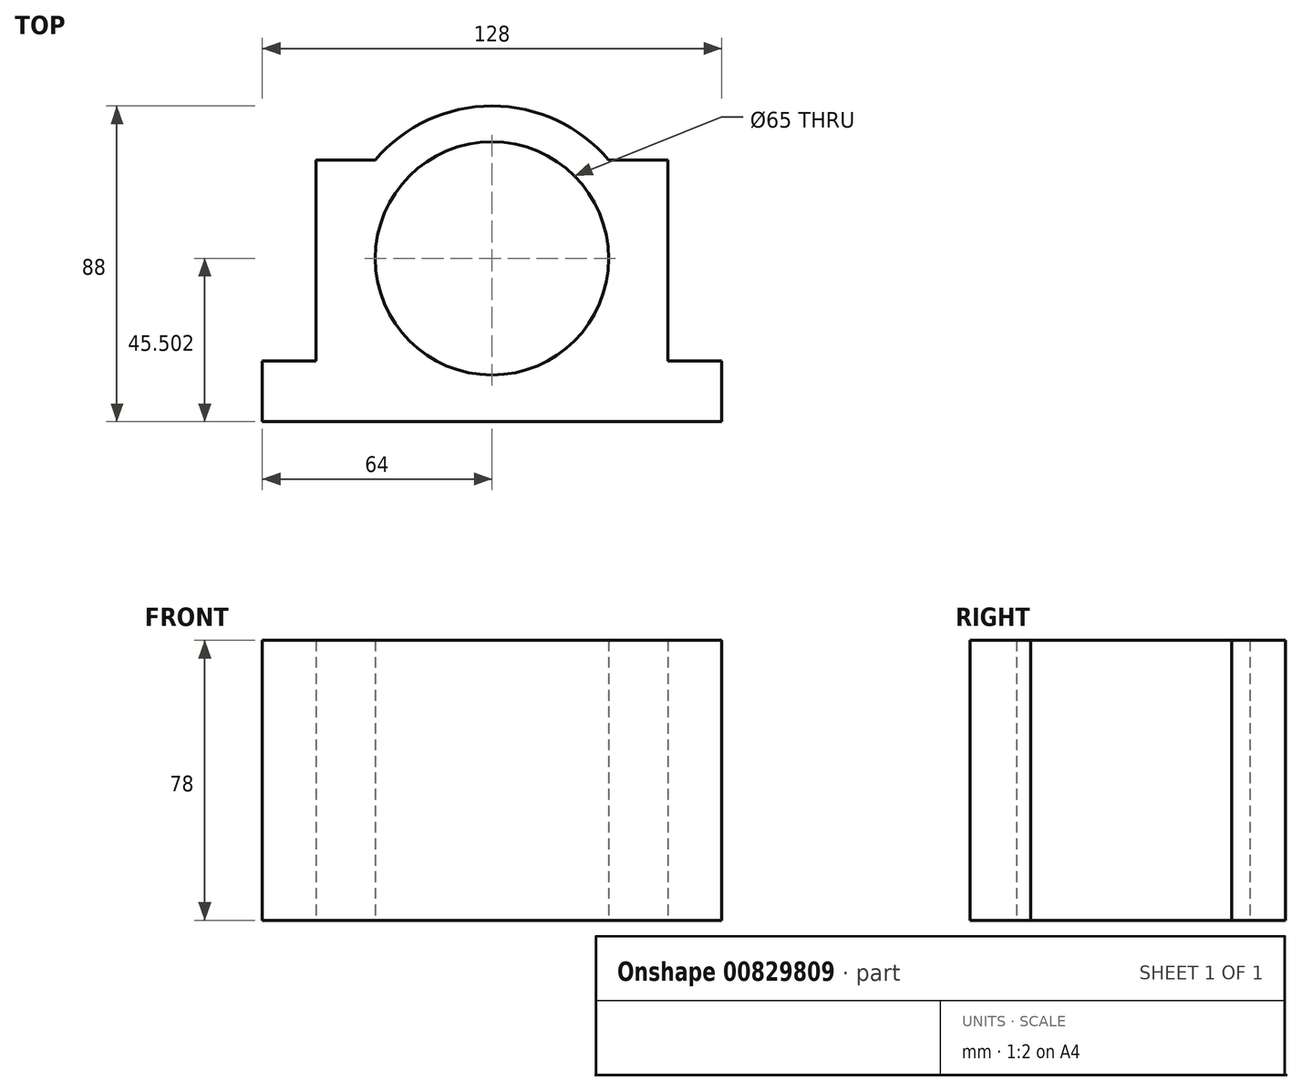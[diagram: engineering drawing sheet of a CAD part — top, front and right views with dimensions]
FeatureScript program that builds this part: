
annotation { "Feature Type Name" : "Feature", "Feature Type Description" : "" }
export const myFeature = defineFeature(function(context is Context, id is Id, definition is map)
    precondition{}
    {
        {
            var Q0;
            Q0=qCreatedBy(makeId("Top.planeOp"),FACE);
            var sketch = newSketch(context, id + "F0", { "sketchPlane" : qUnion([Q0])});
            skLineSegment(sketch, "E0", {"start": v(-64, -45.33) * mm, "end": v(64, -45.33) * mm});
            skLineSegment(sketch, "E1", {"start": v(64, -45.33) * mm, "end": v(64, -28.44) * mm});
            skLineSegment(sketch, "E2", {"start": v(64, -28.44) * mm, "end": v(49, -28.44) * mm});
            skLineSegment(sketch, "E3", {"start": v(-64, -45.33) * mm, "end": v(-64, -28.44) * mm});
            skLineSegment(sketch, "E4", {"start": v(-64, -28.44) * mm, "end": v(-49, -28.44) * mm});
            skLineSegment(sketch, "E5", {"start": v(-49, -28.44) * mm, "end": v(-49, 27.56) * mm});
            skLineSegment(sketch, "E6", {"start": v(-49, 27.56) * mm, "end": v(-32.5, 27.56) * mm});
            skLineSegment(sketch, "E7", {"start": v(49, -28.44) * mm, "end": v(49, 27.56) * mm});
            skLineSegment(sketch, "E8", {"start": v(49, 27.56) * mm, "end": v(32.5, 27.56) * mm});
            skArc(sketch, "E9", {"start": v(32.5, 27.56) * mm, "mid": v(0, 42.67) * mm, "end": v(-32.5, 27.56) * mm});
            skCircle(sketch, "E10", {"center": v(0, 0.17) * mm, "radius": 32.5 * mm});
            skLineSegment(sketch, "E11", {"start": v(32.5, 0.17) * mm, "end": v(32.5, 27.56) * mm, "construction": true});
            skSolve(sketch);
        }
        {
            var Q0;
            Q0=makeQuery(id+"F0.imprint","IMPRINT",FACE,{"disambiguationData":[TD([[makeQuery(id+"F0.imprint","IMPRINT",EDGE,{"derivedFrom":sQuery(id+"F0.wireOp",EDGE,"E0")}),1.0]])]});
            extrude(context, id + "F1", {"entities" : qUnion([Q0]), "depth" : 78 * mm, "offsetDistance" : 25 * mm});
        }
    });
